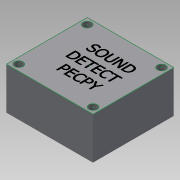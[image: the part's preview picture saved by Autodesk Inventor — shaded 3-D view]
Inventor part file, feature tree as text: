
AUTODESK INVENTOR PART (.ipt)
format: ipt  version: 2015 SP1 (Build 190203100, 203)  size: 99,328 bytes
history: native  units: mm
features: sketch x3, projected_geometry x2, extrude x1
ambient origin geometry x8: Origin, YZ Plane, XZ Plane, XY Plane, X Axis, Y Axis, Z Axis, Center Point
bodies: Solid1 (feature_tree)
feature tree (6):
  extrude  "Extrusion1"  Depth=28.81mm
  sketch  "Sketch2"  dims[d2=3.0mm]
  sketch  "Sketch3"  dims[d6=2.2mm d7=2.2mm d14=20.0mm d16=24.41mm d17=20.0mm d19=26.486mm d22=15.0mm d23=0.0mm]
  sketch  "Sketch1"  dims[d0=30.8864mm d1=28.81mm]
  projected_geometry  "Projected Loop1"
  projected_geometry  "Projected Loop2"
